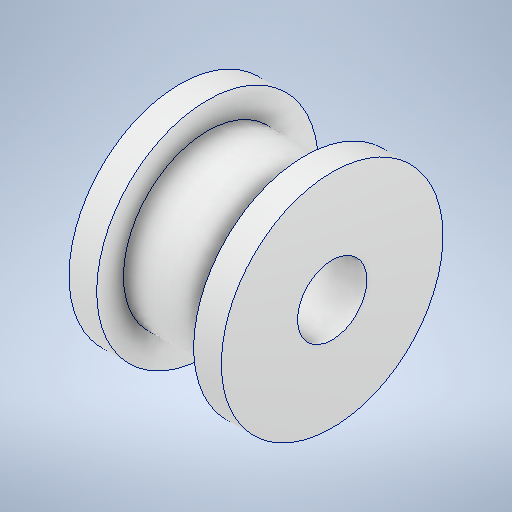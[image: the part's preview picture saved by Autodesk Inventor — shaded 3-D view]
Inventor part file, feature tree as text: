
AUTODESK INVENTOR PART (.ipt)
format: ipt  version: 2025.1 (Build 291241020, 241B)  size: 274,432 bytes
history: native  units: mm
features: revolve x1, mirror x1, sketch x1
ambient origin geometry x8: Origin, YZ Plane, XZ Plane, XY Plane, X Axis, Y Axis, Z Axis, Center Point
bodies: Solid1 (feature_tree)
feature tree (3):
  revolve  "Revolution1"  [1 undecoded]
  mirror  "Mirror2"
  sketch  "Sketch1"  dims[d0=5.5mm d1=3.5mm d2=6.07mm d3=8.0mm d4=2.5mm d5=360.0deg d8=1.0mm]
note: 1 required parameter value undecoded (feature->parameter linkage not recoverable at this tier; creation-order binding heuristic only, values carry confidence <= 0.55)
